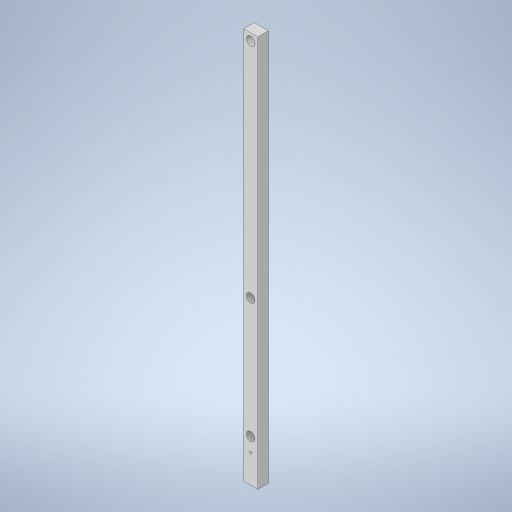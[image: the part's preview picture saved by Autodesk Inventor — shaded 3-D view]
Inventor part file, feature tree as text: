
AUTODESK INVENTOR PART (.ipt)
format: ipt  version: 2024 (Build 280153000, 153)  size: 271,872 bytes
history: native  units: in
note: dims shown in document units (in); Inventor stores cm internally (conversion verified against a paired STEP export)
features: hole x5, sketch x3, extrude x1
ambient origin geometry x8: Origin, YZ Plane, XZ Plane, XY Plane, X Axis, Y Axis, Z Axis, Center Point
bodies: Solid1 (feature_tree)
feature tree (9):
  extrude  "Extrusion1"  Depth=0.1875in
  sketch  "Sketch2"  dims[d2=0.138in d3=6.9363in d4=0.0in]
  hole  "Hole2"  [1 undecoded]
  hole  "Hole3"  [1 undecoded]
  hole  "Hole4"  [1 undecoded]
  hole  "Hole5"  [1 undecoded]
  hole  "Hole6"  [1 undecoded]
  sketch  "Sketch1"  dims[d0=0.25in d1=0.1875in]
  sketch  "Sketch3"  dims[d5=0.125in d6=0.138in d14=0.75in d15=0.138in d16=0.5in d17=0.04in d18=0.1495in d19=0.276in d20=0.279in d21=0.25in d22=0.5635in d23=1.0in d24=0.8108in d25=0.04in d26=0.75in d27=0.375in d28=0.25in d29=0.5635in d30=1.0in d31=0.8108in d32=0.1495in d33=0.75in d34=0.279in d35=0.25in d36=0.5635in d37=1.0in d38=0.8108in d39=0.104in d40=0.104in d41=0.5in d42=0.375in d43=0.25in d44=0.5635in d45=0.5in d46=0.0in d47=3.937in d48=0.138in d49=0.1495in d50=0.25in d51=0.279in d52=0.25in d53=0.5635in d54=0.25in d55=0.0in]
note: 5 required parameter values undecoded (feature->parameter linkage not recoverable at this tier; creation-order binding heuristic only, values carry confidence <= 0.55)
